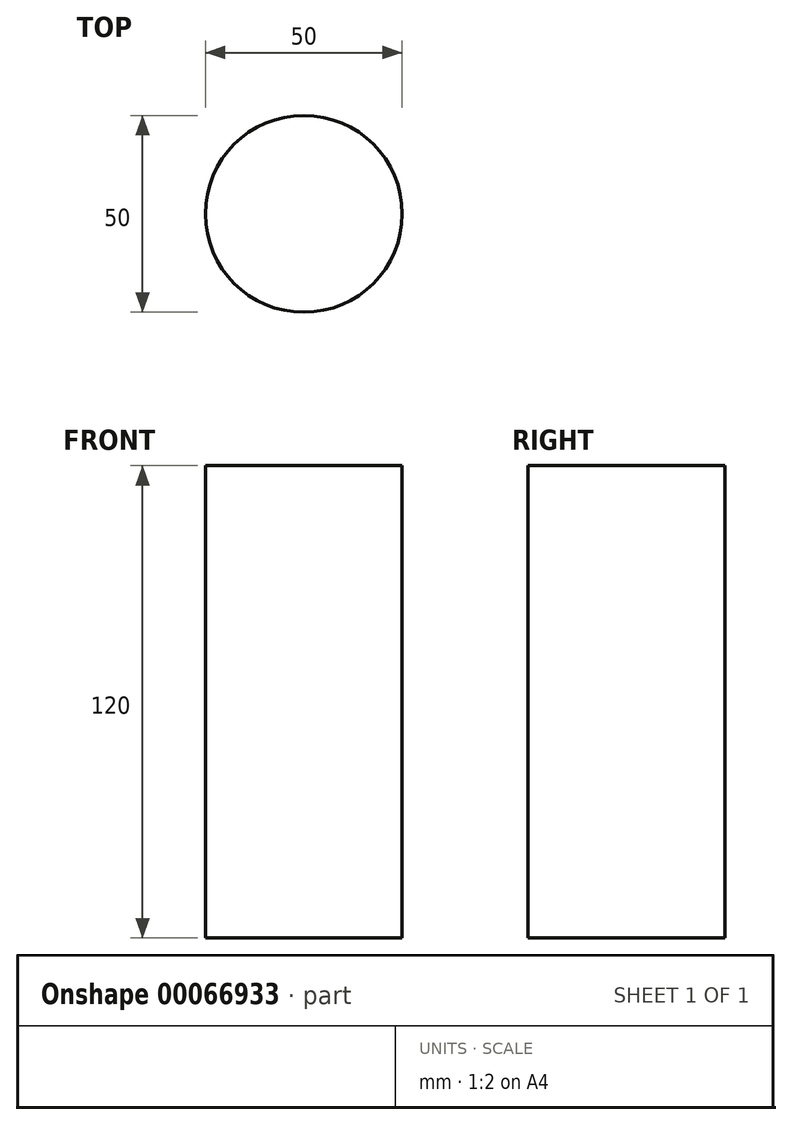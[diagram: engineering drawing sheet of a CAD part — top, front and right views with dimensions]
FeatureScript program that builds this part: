
annotation { "Feature Type Name" : "Feature", "Feature Type Description" : "" }
export const myFeature = defineFeature(function(context is Context, id is Id, definition is map)
    precondition{}
    {
        {
            var Q0;
            Q0=qCreatedBy(makeId("Top.planeOp"),FACE);
            var sketch = newSketch(context, id + "F0", { "sketchPlane" : qUnion([Q0])});
            skCircle(sketch, "E0", {"center": v(0, 0) * mm, "radius": 25 * mm});
            skSolve(sketch);
        }
        {
            var Q0;
            Q0=makeQuery(id+"F0.imprint","IMPRINT",FACE,{"disambiguationData":[TD([[makeQuery(id+"F0.imprint","IMPRINT",EDGE,{"derivedFrom":sQuery(id+"F0.wireOp",EDGE,"E0")}),1.0]])]});
            extrude(context, id + "F1", {"entities" : qUnion([Q0]), "depth" : 120 * mm});
        }
    });
